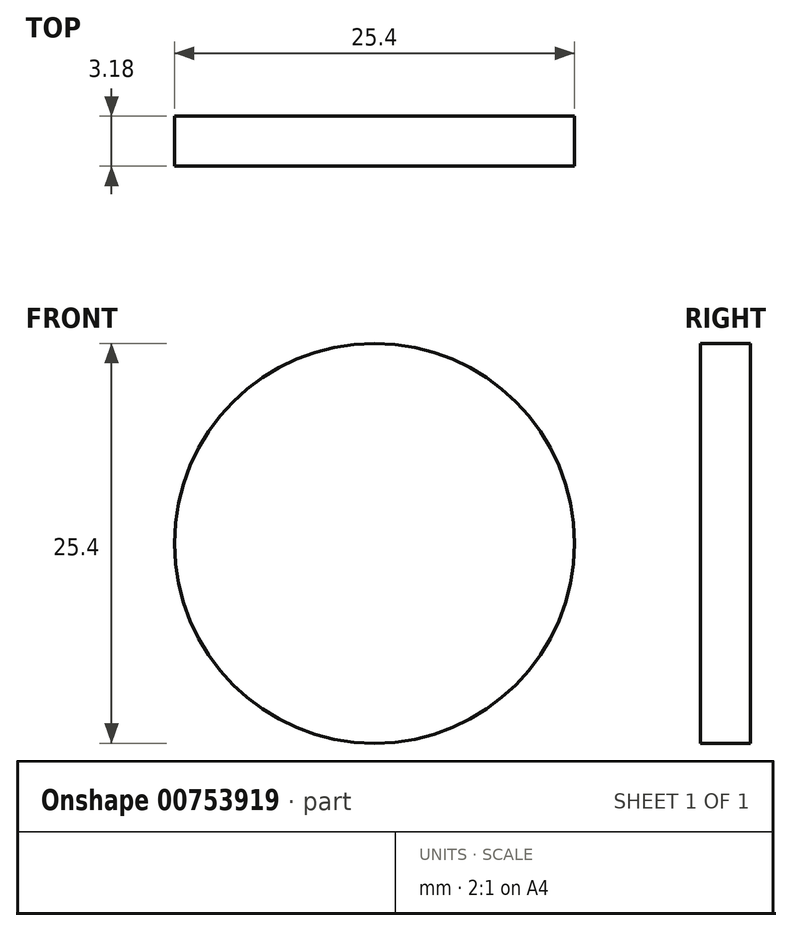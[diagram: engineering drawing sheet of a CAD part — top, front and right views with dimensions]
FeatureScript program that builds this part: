
annotation { "Feature Type Name" : "Feature", "Feature Type Description" : "" }
export const myFeature = defineFeature(function(context is Context, id is Id, definition is map)
    precondition{}
    {
        {
            var Q0;
            Q0=qCreatedBy(makeId("Front.planeOp"),FACE);
            var sketch = newSketch(context, id + "F0", { "sketchPlane" : qUnion([Q0])});
            skCircle(sketch, "E0", {"center": v(0, 0) * mm, "radius": 12.7 * mm});
            skSolve(sketch);
        }
        {
            var Q0;
            Q0=makeQuery(id+"F0.imprint","IMPRINT",FACE,{"disambiguationData":[TD([[makeQuery(id+"F0.imprint","IMPRINT",EDGE,{"derivedFrom":sQuery(id+"F0.wireOp",EDGE,"E0")}),1.0]])]});
            extrude(context, id + "F1", {"entities" : qUnion([Q0]), "depth" : 3.17 * mm, "offsetDistance" : 25.4 * mm});
        }
    });
